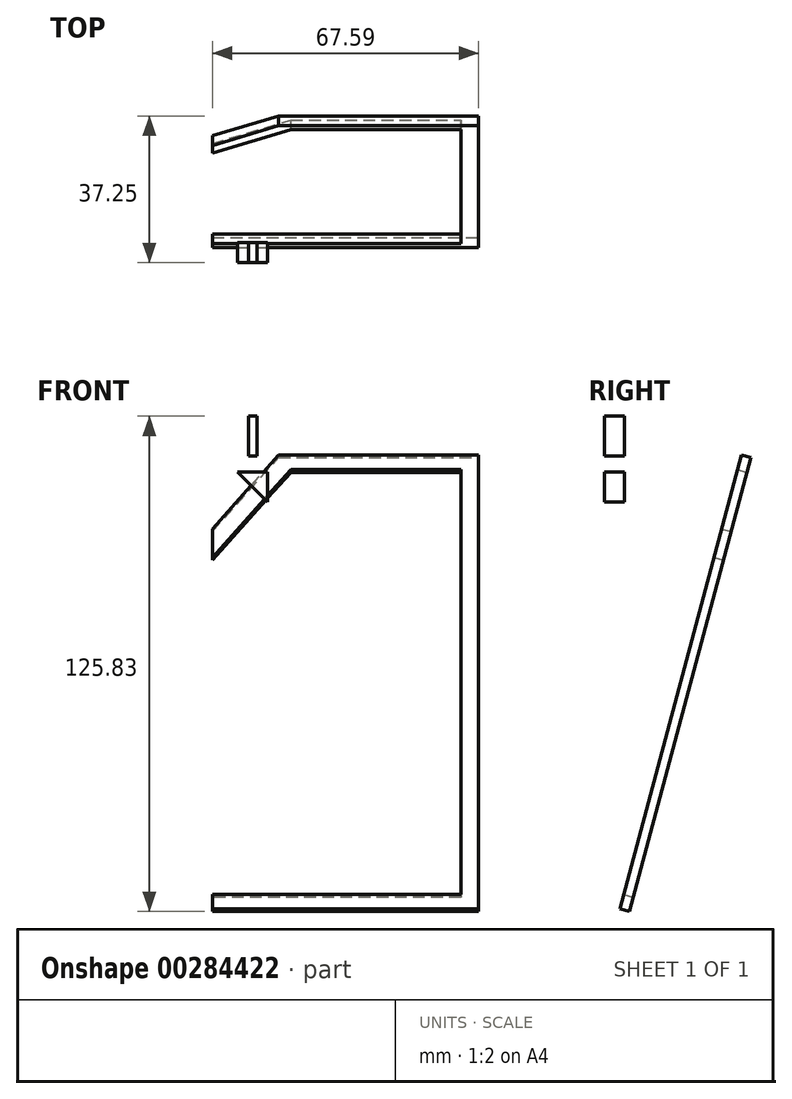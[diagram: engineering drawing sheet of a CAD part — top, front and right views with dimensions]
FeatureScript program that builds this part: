
annotation { "Feature Type Name" : "Feature", "Feature Type Description" : "" }
export const myFeature = defineFeature(function(context is Context, id is Id, definition is map)
    precondition{}
    {
        {
            var Q0;
            Q0=qCreatedBy(makeId("Front.planeOp"),FACE);
            var sketch = newSketch(context, id + "F0", { "sketchPlane" : qUnion([Q0])});
            skLineSegment(sketch, "E0", {"start": v(0, 39.74) * mm, "end": v(19.95, 62.78) * mm});
            skLineSegment(sketch, "E1", {"start": v(19.95, 62.78) * mm, "end": v(63.13, 62.78) * mm});
            skLineSegment(sketch, "E2", {"start": v(63.13, 62.78) * mm, "end": v(63.13, -48.98) * mm});
            skLineSegment(sketch, "E3", {"start": v(0, 47.24) * mm, "end": v(16.8, 66.64) * mm});
            skLineSegment(sketch, "E4", {"start": v(16.8, 66.64) * mm, "end": v(67.6, 66.64) * mm});
            skLineSegment(sketch, "E5", {"start": v(67.6, 66.64) * mm, "end": v(67.6, -52.74) * mm});
            skLineSegment(sketch, "E6", {"start": v(63.13, -48.98) * mm, "end": v(0, -48.98) * mm});
            skLineSegment(sketch, "E7", {"start": v(0, -48.98) * mm, "end": v(0, -52.74) * mm});
            skLineSegment(sketch, "E8", {"start": v(0, -52.74) * mm, "end": v(67.6, -52.74) * mm});
            skLineSegment(sketch, "E9", {"start": v(0, 47.24) * mm, "end": v(0, 39.74) * mm});
            skSolve(sketch);
        }
        {
            var Q0;
            Q0 = qSketchRegion(id + "F0", true);
            extrude(context, id + "F1", {"entities" : qUnion([Q0]), "endBound" : BoundingType.SYMMETRIC, "depth" : 2.54 * mm});
        }
        {
            var Q0;
            Q0=makeQuery(id+"F1.opExtrude","SWEPT_BODY",BODY,{"disambiguationData":[OSD([sQuery(id+"F0.wireOp",EDGE,"E0"),sQuery(id+"F0.wireOp",EDGE,"E1"),sQuery(id+"F0.wireOp",EDGE,"E2"),sQuery(id+"F0.wireOp",EDGE,"E3"),sQuery(id+"F0.wireOp",EDGE,"E4"),sQuery(id+"F0.wireOp",EDGE,"E5"),sQuery(id+"F0.wireOp",EDGE,"E6"),sQuery(id+"F0.wireOp",EDGE,"E7"),sQuery(id+"F0.wireOp",EDGE,"E8"),sQuery(id+"F0.wireOp",EDGE,"E9")])]});
            var Q1;
            Q1=makeQuery(id+"F1.opExtrude","CAP_EDGE",EDGE,{"disambiguationData":[OSD([sQuery(id+"F0.wireOp",EDGE,"E8")])],"isStart":true});
            transform(context, id + "F2", {"entities" : qUnion([Q0]), "transformType" : TransformType.ROTATION, "transformAxis" : qUnion([Q1]), "angle" : 15 * degree, "oppositeDirection" : true, "makeCopy" : false});
        }
        {
            var Q0;
            Q0=qCreatedBy(makeId("Front.planeOp"),FACE);
            var sketch = newSketch(context, id + "F3", { "sketchPlane" : qUnion([Q0])});
            skLineSegment(sketch, "E10", {"start": v(6.42, 58.95) * mm, "end": v(14.04, 58.95) * mm});
            skLineSegment(sketch, "E11", {"start": v(14.04, 58.95) * mm, "end": v(14.04, 51.33) * mm});
            skLineSegment(sketch, "E12", {"start": v(14.04, 51.33) * mm, "end": v(6.42, 58.95) * mm});
            skText(sketch, "E13", { "text": "I", "fontName": "OpenSans-Bold.ttf"});
            const initialGuessF3  = {"E13": [0.0079, 0.06302, 1, 0, 0.01016]};
            skSetInitialGuess(sketch, initialGuessF3);
            skSolve(sketch);
        }
        {
            var Q0;
            Q0 = qSketchRegion(id + "F3", true);
            extrude(context, id + "F4", {"entities" : qUnion([Q0]), "depth" : 5.08 * mm});
        }
    });
